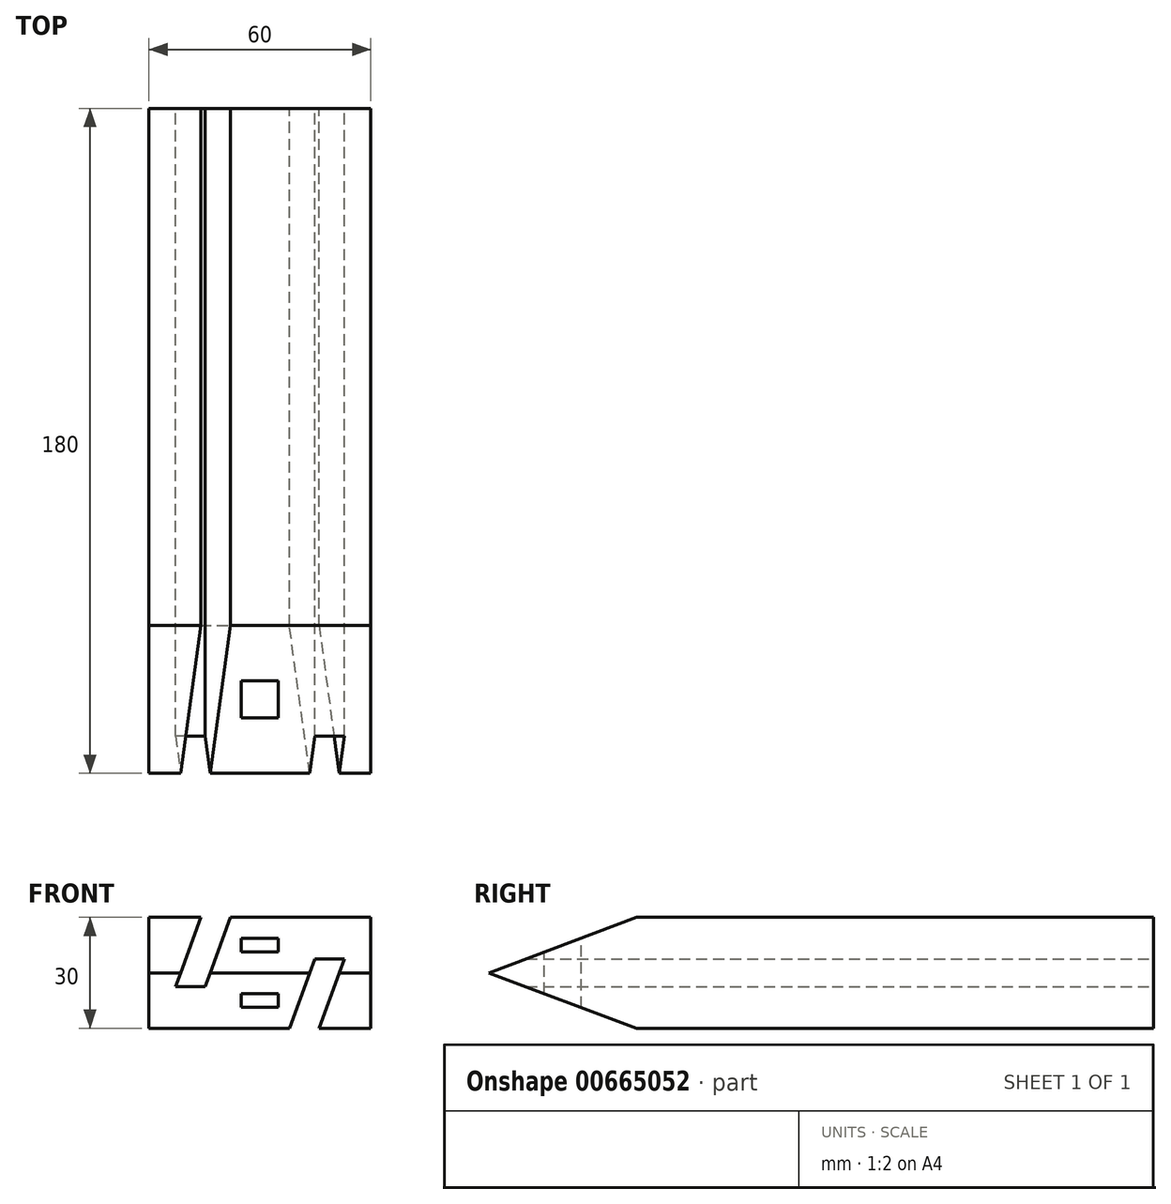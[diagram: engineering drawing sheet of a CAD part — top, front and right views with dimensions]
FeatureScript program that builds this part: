
annotation { "Feature Type Name" : "Feature", "Feature Type Description" : "" }
export const myFeature = defineFeature(function(context is Context, id is Id, definition is map)
    precondition{}
    {
        {
            var Q0;
            Q0=qCreatedBy(makeId("Front.planeOp"),FACE);
            var sketch = newSketch(context, id + "F0", { "sketchPlane" : qUnion([Q0])});
            skLineSegment(sketch, "E0.bottom", {"start": v(30, 15) * mm, "end": v(-30, 15) * mm});
            skLineSegment(sketch, "E0.top", {"start": v(30, -15) * mm, "end": v(-30, -15) * mm});
            skLineSegment(sketch, "E0.left", {"start": v(30, 15) * mm, "end": v(30, -15) * mm});
            skLineSegment(sketch, "E0.right", {"start": v(-30, 15) * mm, "end": v(-30, -15) * mm});
            skLineSegment(sketch, "E1", {"start": v(-8, 15) * mm, "end": v(-14.84, -3.8) * mm});
            skLineSegment(sketch, "E2", {"start": v(-14.84, -3.8) * mm, "end": v(-22.84, -3.8) * mm});
            skLineSegment(sketch, "E3", {"start": v(-22.84, -3.8) * mm, "end": v(-16, 15) * mm});
            skLineSegment(sketch, "E4", {"start": v(16, -15) * mm, "end": v(22.84, 3.8) * mm});
            skLineSegment(sketch, "E5", {"start": v(22.84, 3.8) * mm, "end": v(14.84, 3.8) * mm});
            skLineSegment(sketch, "E6", {"start": v(14.84, 3.8) * mm, "end": v(8, -15) * mm});
            skSolve(sketch);
        }
        {
            var Q0;
            {var subQ3=sQuery(id+"F0.wireOp",EDGE,"E0.left");Q0=makeQuery(id+"F0.imprint","IMPRINT",FACE,{"disambiguationData":[TD([[makeQuery(id+"F0.imprint","IMPRINT",EDGE,{"derivedFrom":subQ3}),-1.0]])]});}
            extrude(context, id + "F1", {"entities" : qUnion([Q0]), "endBound" : BoundingType.SYMMETRIC, "depth" : 320 * mm, "offsetDistance" : 25 * mm});
        }
        {
            var Q0;
            {var subQ0=sQuery(id+"F0.wireOp",EDGE,"E0.bottom");Q0=makeQuery(id+"F1.opExtrude","SWEPT_FACE",FACE,{"disambiguationData":[OSD([subQ0]),TDD([makeQuery(id+"F0.imprint","IMPRINT",EDGE,{"disambiguationData":[TD([[makeQuery(id+"F0.imprint","INTERSECT",VERTEX,{"derivedFrom":[subQ0,sQuery(id+"F0.wireOp",EDGE,"E0.left")]}),-1.0]])],"derivedFrom":subQ0})])]});}
            var sketch = newSketch(context, id + "F2", { "sketchPlane" : qUnion([Q0])});
            skLineSegment(sketch, "E7.bottom", {"start": v(5, 5) * mm, "end": v(-5, 5) * mm});
            skLineSegment(sketch, "E7.top", {"start": v(5, -5) * mm, "end": v(-5, -5) * mm});
            skLineSegment(sketch, "E7.left", {"start": v(5, 5) * mm, "end": v(5, -5) * mm});
            skLineSegment(sketch, "E7.right", {"start": v(-5, 5) * mm, "end": v(-5, -5) * mm});
            skPoint(sketch, "E7.middle", {"position": v(0, 0) * mm});
            skSolve(sketch);
        }
        {
            var Q0;
            Q0=makeQuery(id+"F2.imprint","IMPRINT",FACE,{"disambiguationData":[TD([[makeQuery(id+"F2.imprint","IMPRINT",EDGE,{"derivedFrom":sQuery(id+"F2.wireOp",EDGE,"E7.bottom")}),1.0]])]});
            extrude(context, id + "F3", {"entities" : qUnion([Q0]), "operationType" : NewBodyOperationType.REMOVE, "oppositeDirection" : true, "depth" : 60 * mm, "offsetDistance" : 25 * mm});
        }
        {
            var Q0;
            Q0=makeQuery(id+"F1.opExtrude","SWEPT_FACE",FACE,{"disambiguationData":[OSD([sQuery(id+"F0.wireOp",EDGE,"E0.left")])]});
            var sketch = newSketch(context, id + "F4", { "sketchPlane" : qUnion([Q0])});
            skLineSegment(sketch, "E8", {"start": v(0, 15) * mm, "end": v(0, -15) * mm});
            skLineSegment(sketch, "E9", {"start": v(0, -15) * mm, "end": v(20, -15) * mm});
            skLineSegment(sketch, "E10", {"start": v(20, -15) * mm, "end": v(20, 15) * mm});
            skLineSegment(sketch, "E11", {"start": v(0, 0) * mm, "end": v(-20, 0) * mm});
            skLineSegment(sketch, "E12", {"start": v(-20, 0) * mm, "end": v(20, -15) * mm});
            skLineSegment(sketch, "E13", {"start": v(20, 15) * mm, "end": v(-20, 0) * mm});
            skSolve(sketch);
        }
        {
            var Q0;
            {var subQ5=sQuery(id+"F0.wireOp",EDGE,"E0.left");var subQ8=makeQuery(id+"F1.opExtrude","CAP_EDGE",EDGE,{"disambiguationData":[OSD([subQ5])],"isStart":false});Q0=makeQuery(id+"F4.imprint","IMPRINT",FACE,{"disambiguationData":[TD([[makeQuery(id+"F4.imprint","IMPRINT",EDGE,{"derivedFrom":subQ8}),1.0]])]});}
            var Q1;
            {var subQ0=sQuery(id+"F4.wireOp",EDGE,"E8");var subQ3=sQuery(id+"F4.wireOp",EDGE,"E13");var subQ4=makeQuery(id+"F4.imprint","INTERSECT",VERTEX,{"derivedFrom":[subQ0,subQ3]});Q1=makeQuery(id+"F4.imprint","IMPRINT",FACE,{"disambiguationData":[TD([[makeQuery(id+"F4.imprint","IMPRINT",EDGE,{"disambiguationData":[TD([[subQ4,1.0]])],"derivedFrom":subQ0}),1.0]])]});}
            var Q2;
            {var subQ0=sQuery(id+"F4.wireOp",EDGE,"E9");Q2=makeQuery(id+"F4.imprint","IMPRINT",FACE,{"disambiguationData":[TD([[makeQuery(id+"F4.imprint","IMPRINT",EDGE,{"derivedFrom":subQ0}),1.0]])]});}
            extrude(context, id + "F5", {"entities" : qUnion([Q0, Q1, Q2]), "operationType" : NewBodyOperationType.REMOVE, "oppositeDirection" : true, "depth" : 60 * mm, "offsetDistance" : 25 * mm});
        }
    });
